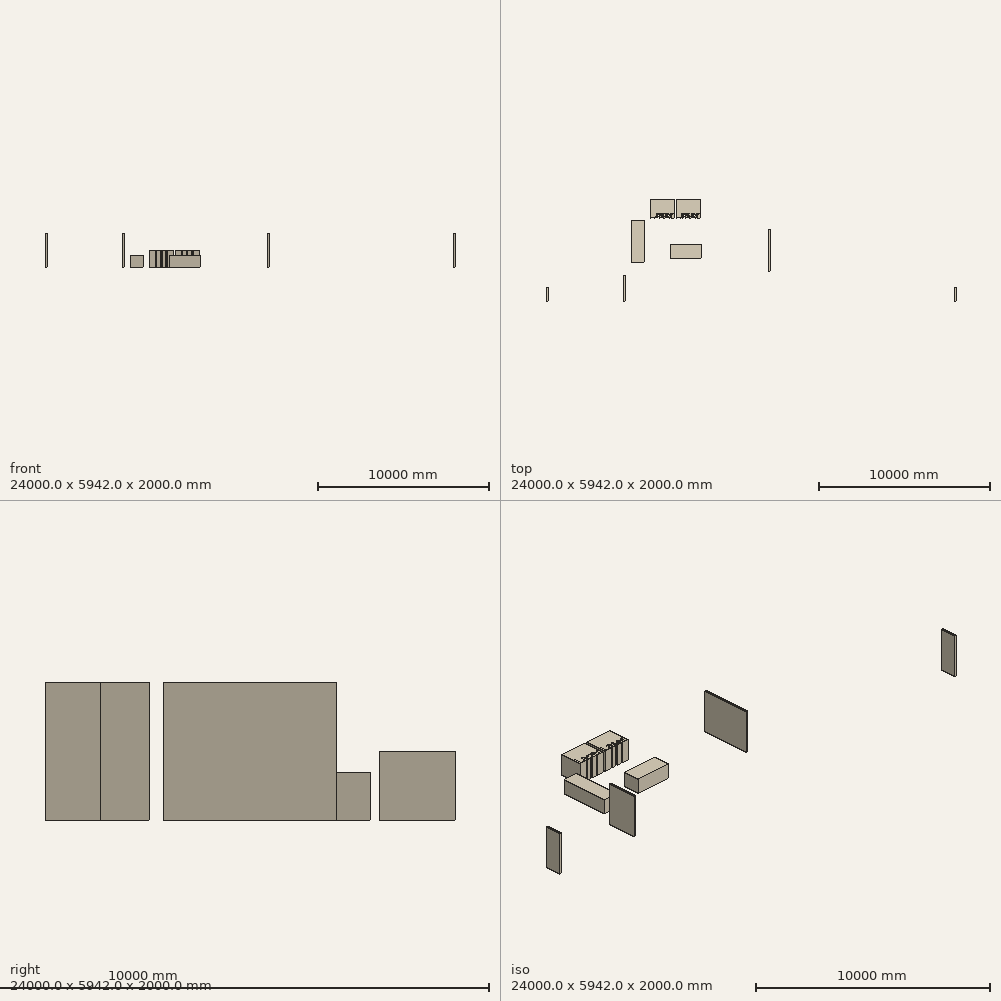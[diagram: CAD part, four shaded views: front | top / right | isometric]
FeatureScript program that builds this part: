
annotation { "Feature Type Name" : "Feature", "Feature Type Description" : "" }
export const myFeature = defineFeature(function(context is Context, id is Id, definition is map)
    precondition{}
    {
        {
            var Q0;
            Q0=qCreatedBy(makeId("Top.planeOp"),FACE);
            var sketch = newSketch(context, id + "F0", { "sketchPlane" : qUnion([Q0])});
            skLineSegment(sketch, "E0.bottom", {"start": v(-12000, 3350) * mm, "end": v(12000, 3350) * mm});
            skLineSegment(sketch, "E0.top", {"start": v(-12000, -3350) * mm, "end": v(12000, -3350) * mm});
            skLineSegment(sketch, "E0.left", {"start": v(-12000, 3350) * mm, "end": v(-12000, -3350) * mm});
            skLineSegment(sketch, "E0.right", {"start": v(12000, 3350) * mm, "end": v(12000, -3350) * mm});
            skPoint(sketch, "E0.middle", {"position": v(0, 0) * mm});
            skLineSegment(sketch, "E1.bottom", {"start": v(-11200, -3350) * mm, "end": v(-8700, -3350) * mm});
            skLineSegment(sketch, "E1.top", {"start": v(-11200, -3250) * mm, "end": v(-8700, -3250) * mm});
            skLineSegment(sketch, "E1.left", {"start": v(-11200, -3350) * mm, "end": v(-11200, -3250) * mm});
            skLineSegment(sketch, "E1.right", {"start": v(-8700, -3350) * mm, "end": v(-8700, -3250) * mm});
            skLineSegment(sketch, "E2.bottom", {"start": v(-12000, -2850) * mm, "end": v(-11900, -2850) * mm});
            skLineSegment(sketch, "E2.top", {"start": v(-12000, -2050) * mm, "end": v(-11900, -2050) * mm});
            skLineSegment(sketch, "E2.left", {"start": v(-12000, -2850) * mm, "end": v(-12000, -2050) * mm});
            skLineSegment(sketch, "E2.right", {"start": v(-11900, -2850) * mm, "end": v(-11900, -2050) * mm});
            skLineSegment(sketch, "E3.bottom", {"start": v(-11200, 3350) * mm, "end": v(-8700, 3350) * mm});
            skLineSegment(sketch, "E3.top", {"start": v(-11200, 3250) * mm, "end": v(-8700, 3250) * mm});
            skLineSegment(sketch, "E3.left", {"start": v(-11200, 3350) * mm, "end": v(-11200, 3250) * mm});
            skLineSegment(sketch, "E3.right", {"start": v(-8700, 3350) * mm, "end": v(-8700, 3250) * mm});
            skLineSegment(sketch, "E4.bottom", {"start": v(1200, -3350) * mm, "end": v(3700, -3350) * mm});
            skLineSegment(sketch, "E4.top", {"start": v(1200, -3250) * mm, "end": v(3700, -3250) * mm});
            skLineSegment(sketch, "E4.left", {"start": v(1200, -3350) * mm, "end": v(1200, -3250) * mm});
            skLineSegment(sketch, "E4.right", {"start": v(3700, -3350) * mm, "end": v(3700, -3250) * mm});
            skLineSegment(sketch, "E5.bottom", {"start": v(3900, -3350) * mm, "end": v(4700, -3350) * mm});
            skLineSegment(sketch, "E5.top", {"start": v(3900, -3250) * mm, "end": v(4700, -3250) * mm});
            skLineSegment(sketch, "E5.left", {"start": v(3900, -3350) * mm, "end": v(3900, -3250) * mm});
            skLineSegment(sketch, "E5.right", {"start": v(4700, -3350) * mm, "end": v(4700, -3250) * mm});
            skLineSegment(sketch, "E6.bottom", {"start": v(12000, -2050) * mm, "end": v(11900, -2050) * mm});
            skLineSegment(sketch, "E6.top", {"start": v(12000, -2850) * mm, "end": v(11900, -2850) * mm});
            skLineSegment(sketch, "E6.left", {"start": v(12000, -2050) * mm, "end": v(12000, -2850) * mm});
            skLineSegment(sketch, "E6.right", {"start": v(11900, -2050) * mm, "end": v(11900, -2850) * mm});
            skLineSegment(sketch, "E7", {"start": v(-7400, 3350) * mm, "end": v(-7400, -3350) * mm});
            skLineSegment(sketch, "E8", {"start": v(1000, 3350) * mm, "end": v(1000, -3350) * mm});
            skLineSegment(sketch, "E9.bottom", {"start": v(-3207.33, -2950.98) * mm, "end": v(-1707.33, -2950.98) * mm});
            skLineSegment(sketch, "E9.top", {"start": v(-3207.33, -1950.98) * mm, "end": v(-1707.33, -1950.98) * mm});
            skLineSegment(sketch, "E9.left", {"start": v(-3207.33, -2950.98) * mm, "end": v(-3207.33, -1950.98) * mm});
            skLineSegment(sketch, "E9.right", {"start": v(-1707.33, -2950.98) * mm, "end": v(-1707.33, -1950.98) * mm});
            skText(sketch, "E10", { "text": "Lathe", "fontName": "OpenSans-Regular.ttf"});
            skLineSegment(sketch, "E11.bottom", {"start": v(-5928.56, 3091.98) * mm, "end": v(-4528.56, 3091.98) * mm});
            skLineSegment(sketch, "E11.top", {"start": v(-5928.56, 1991.98) * mm, "end": v(-4528.56, 1991.98) * mm});
            skLineSegment(sketch, "E11.left", {"start": v(-5928.56, 3091.98) * mm, "end": v(-5928.56, 1991.98) * mm});
            skLineSegment(sketch, "E11.right", {"start": v(-4528.56, 3091.98) * mm, "end": v(-4528.56, 1991.98) * mm});
            skText(sketch, "E12", { "text": "Laser", "fontName": "OpenSans-Regular.ttf"});
            skLineSegment(sketch, "E13.bottom", {"start": v(-4412.76, 3091.98) * mm, "end": v(-3012.76, 3091.98) * mm});
            skLineSegment(sketch, "E13.top", {"start": v(-4412.76, 1991.98) * mm, "end": v(-3012.76, 1991.98) * mm});
            skLineSegment(sketch, "E13.left", {"start": v(-4412.76, 3091.98) * mm, "end": v(-4412.76, 1991.98) * mm});
            skLineSegment(sketch, "E13.right", {"start": v(-3012.76, 3091.98) * mm, "end": v(-3012.76, 1991.98) * mm});
            skText(sketch, "E14", { "text": "Laser", "fontName": "OpenSans-Regular.ttf"});
            skLineSegment(sketch, "E15.bottom", {"start": v(-1450.58, -1150.98) * mm, "end": v(549.42, -1150.98) * mm});
            skLineSegment(sketch, "E15.top", {"start": v(-1450.58, -2950.98) * mm, "end": v(549.42, -2950.98) * mm});
            skLineSegment(sketch, "E15.left", {"start": v(-1450.58, -1150.98) * mm, "end": v(-1450.58, -2950.98) * mm});
            skLineSegment(sketch, "E15.right", {"start": v(549.42, -1150.98) * mm, "end": v(549.42, -2950.98) * mm});
            skText(sketch, "E16", { "text": "Mill", "fontName": "OpenSans-Regular.ttf"});
            skLineSegment(sketch, "E17.bottom", {"start": v(-1450.58, -1150.98) * mm, "end": v(549.42, -1150.98) * mm, "construction": true});
            skLineSegment(sketch, "E17.top", {"start": v(-1450.58, 349.02) * mm, "end": v(549.42, 349.02) * mm, "construction": true});
            skLineSegment(sketch, "E17.left", {"start": v(-1450.58, -1150.98) * mm, "end": v(-1450.58, 349.02) * mm, "construction": true});
            skLineSegment(sketch, "E17.right", {"start": v(549.42, -1150.98) * mm, "end": v(549.42, 349.02) * mm, "construction": true});
            skLineSegment(sketch, "E18.bottom", {"start": v(-3207.33, -1950.98) * mm, "end": v(-1707.33, -1950.98) * mm, "construction": true});
            skLineSegment(sketch, "E18.top", {"start": v(-3207.33, -450.98) * mm, "end": v(-1707.33, -450.98) * mm, "construction": true});
            skLineSegment(sketch, "E18.left", {"start": v(-3207.33, -1950.98) * mm, "end": v(-3207.33, -450.98) * mm, "construction": true});
            skLineSegment(sketch, "E18.right", {"start": v(-1707.33, -1950.98) * mm, "end": v(-1707.33, -450.98) * mm, "construction": true});
            skLineSegment(sketch, "E19.bottom", {"start": v(-773.2, 3091.98) * mm, "end": v(726.8, 3091.98) * mm});
            skLineSegment(sketch, "E19.top", {"start": v(-773.2, 1591.98) * mm, "end": v(726.8, 1591.98) * mm});
            skLineSegment(sketch, "E19.left", {"start": v(-773.2, 3091.98) * mm, "end": v(-773.2, 1591.98) * mm});
            skLineSegment(sketch, "E19.right", {"start": v(726.8, 3091.98) * mm, "end": v(726.8, 1591.98) * mm});
            skLineSegment(sketch, "E20.bottom", {"start": v(-773.2, 1591.98) * mm, "end": v(726.8, 1591.98) * mm, "construction": true});
            skLineSegment(sketch, "E20.top", {"start": v(-773.2, 91.98) * mm, "end": v(726.8, 91.98) * mm, "construction": true});
            skLineSegment(sketch, "E20.left", {"start": v(-773.2, 1591.98) * mm, "end": v(-773.2, 91.98) * mm, "construction": true});
            skLineSegment(sketch, "E20.right", {"start": v(726.8, 1591.98) * mm, "end": v(726.8, 91.98) * mm, "construction": true});
            skText(sketch, "E21", { "text": "CNC", "fontName": "OpenSans-Regular.ttf"});
            skLineSegment(sketch, "E22.bottom", {"start": v(-6911.27, -2908.56) * mm, "end": v(-4472.87, -2908.56) * mm});
            skLineSegment(sketch, "E22.top", {"start": v(-6911.27, -2146.56) * mm, "end": v(-4472.87, -2146.56) * mm});
            skLineSegment(sketch, "E22.left", {"start": v(-6911.27, -2908.56) * mm, "end": v(-6911.27, -2146.56) * mm});
            skLineSegment(sketch, "E22.right", {"start": v(-4472.87, -2908.56) * mm, "end": v(-4472.87, -2146.56) * mm});
            skLineSegment(sketch, "E23.bottom", {"start": v(-7007.98, 1864.72) * mm, "end": v(-6245.98, 1864.72) * mm});
            skLineSegment(sketch, "E23.top", {"start": v(-7007.98, -573.68) * mm, "end": v(-6245.98, -573.68) * mm});
            skLineSegment(sketch, "E23.left", {"start": v(-7007.98, 1864.72) * mm, "end": v(-7007.98, -573.68) * mm});
            skLineSegment(sketch, "E23.right", {"start": v(-6245.98, 1864.72) * mm, "end": v(-6245.98, -573.68) * mm});
            skLineSegment(sketch, "E24.bottom", {"start": v(-2789.45, 3077.16) * mm, "end": v(-960.65, 3077.16) * mm});
            skLineSegment(sketch, "E24.top", {"start": v(-2789.45, 2315.16) * mm, "end": v(-960.65, 2315.16) * mm});
            skLineSegment(sketch, "E24.left", {"start": v(-2789.45, 3077.16) * mm, "end": v(-2789.45, 2315.16) * mm});
            skLineSegment(sketch, "E24.right", {"start": v(-960.65, 3077.16) * mm, "end": v(-960.65, 2315.16) * mm});
            skText(sketch, "E25", { "text": "Desk", "fontName": "OpenSans-Regular.ttf"});
            skText(sketch, "E26", { "text": "Chop", "fontName": "OpenSans-Regular.ttf"});
            skLineSegment(sketch, "E27.bottom", {"start": v(-4742.76, 474.12) * mm, "end": v(-2913.96, 474.12) * mm});
            skLineSegment(sketch, "E27.top", {"start": v(-4742.76, -338.68) * mm, "end": v(-2913.96, -338.68) * mm});
            skLineSegment(sketch, "E27.left", {"start": v(-4742.76, 474.12) * mm, "end": v(-4742.76, -338.68) * mm});
            skLineSegment(sketch, "E27.right", {"start": v(-2913.96, 474.12) * mm, "end": v(-2913.96, -338.68) * mm});
            skLineSegment(sketch, "E28.bottom", {"start": v(-7400, -1350) * mm, "end": v(-7500, -1350) * mm});
            skLineSegment(sketch, "E28.top", {"start": v(-7400, -2850) * mm, "end": v(-7500, -2850) * mm});
            skLineSegment(sketch, "E28.left", {"start": v(-7400, -1350) * mm, "end": v(-7400, -2850) * mm});
            skLineSegment(sketch, "E28.right", {"start": v(-7500, -1350) * mm, "end": v(-7500, -2850) * mm});
            skLineSegment(sketch, "E29.bottom", {"start": v(1000, 1365.62) * mm, "end": v(1100, 1365.62) * mm});
            skLineSegment(sketch, "E29.top", {"start": v(1000, -1134.38) * mm, "end": v(1100, -1134.38) * mm});
            skLineSegment(sketch, "E29.left", {"start": v(1000, 1365.62) * mm, "end": v(1000, -1134.38) * mm});
            skLineSegment(sketch, "E29.right", {"start": v(1100, 1365.62) * mm, "end": v(1100, -1134.38) * mm});
            skLineSegment(sketch, "E30.bottom", {"start": v(12000, -3350) * mm, "end": v(10500, -3350) * mm});
            skLineSegment(sketch, "E30.top", {"start": v(12000, -1850) * mm, "end": v(10500, -1850) * mm});
            skLineSegment(sketch, "E30.left", {"start": v(12000, -3350) * mm, "end": v(12000, -1850) * mm});
            skLineSegment(sketch, "E30.right", {"start": v(10500, -3350) * mm, "end": v(10500, -1850) * mm});
            skLineSegment(sketch, "E31.bottom", {"start": v(10500, -1850) * mm, "end": v(5500, -1850) * mm});
            skLineSegment(sketch, "E31.top", {"start": v(10500, -3350) * mm, "end": v(5500, -3350) * mm});
            skLineSegment(sketch, "E31.left", {"start": v(10500, -1850) * mm, "end": v(10500, -3350) * mm});
            skLineSegment(sketch, "E31.right", {"start": v(5500, -1850) * mm, "end": v(5500, -3350) * mm});
            skLineSegment(sketch, "E32", {"start": v(5800, -1850) * mm, "end": v(5800, -3350) * mm});
            skLineSegment(sketch, "E33.1.0.0", {"start": v(6100, -1850) * mm, "end": v(6100, -3350) * mm});
            skLineSegment(sketch, "E33.2.0.0", {"start": v(6400, -1850) * mm, "end": v(6400, -3350) * mm});
            skLineSegment(sketch, "E33.3.0.0", {"start": v(6700, -1850) * mm, "end": v(6700, -3350) * mm});
            skLineSegment(sketch, "E33.4.0.0", {"start": v(7000, -1850) * mm, "end": v(7000, -3350) * mm});
            skLineSegment(sketch, "E33.5.0.0", {"start": v(7300, -1850) * mm, "end": v(7300, -3350) * mm});
            skLineSegment(sketch, "E33.6.0.0", {"start": v(7600, -1850) * mm, "end": v(7600, -3350) * mm});
            skLineSegment(sketch, "E33.7.0.0", {"start": v(7900, -1850) * mm, "end": v(7900, -3350) * mm});
            skLineSegment(sketch, "E33.8.0.0", {"start": v(8200, -1850) * mm, "end": v(8200, -3350) * mm});
            skLineSegment(sketch, "E33.9.0.0", {"start": v(8500, -1850) * mm, "end": v(8500, -3350) * mm});
            skLineSegment(sketch, "E33.10.0.0", {"start": v(8800, -1850) * mm, "end": v(8800, -3350) * mm});
            skLineSegment(sketch, "E33.11.0.0", {"start": v(9100, -1850) * mm, "end": v(9100, -3350) * mm});
            skLineSegment(sketch, "E33.12.0.0", {"start": v(9400, -1850) * mm, "end": v(9400, -3350) * mm});
            skLineSegment(sketch, "E33.13.0.0", {"start": v(9700, -1850) * mm, "end": v(9700, -3350) * mm});
            skLineSegment(sketch, "E33.14.0.0", {"start": v(10000, -1850) * mm, "end": v(10000, -3350) * mm});
            skLineSegment(sketch, "E33.15.0.0", {"start": v(10300, -1850) * mm, "end": v(10300, -3350) * mm});
            skLineSegment(sketch, "E33.direction1", {"start": v(5800, -3350) * mm, "end": v(6100, -3350) * mm, "construction": true});
            skLineSegment(sketch, "E34.bottom", {"start": v(-8720.08, 3699.81) * mm, "end": v(-7720.08, 3699.81) * mm});
            skLineSegment(sketch, "E34.top", {"start": v(-8720.08, 2499.81) * mm, "end": v(-7720.08, 2499.81) * mm});
            skLineSegment(sketch, "E34.left", {"start": v(-8720.08, 3699.81) * mm, "end": v(-8720.08, 2499.81) * mm});
            skLineSegment(sketch, "E34.right", {"start": v(-7720.08, 3699.81) * mm, "end": v(-7720.08, 2499.81) * mm});
            skLineSegment(sketch, "E35.bottom", {"start": v(-8720.08, 2404.3) * mm, "end": v(-7720.08, 2404.3) * mm});
            skLineSegment(sketch, "E35.top", {"start": v(-8720.08, 1204.3) * mm, "end": v(-7720.08, 1204.3) * mm});
            skLineSegment(sketch, "E35.left", {"start": v(-8720.08, 2404.3) * mm, "end": v(-8720.08, 1204.3) * mm});
            skLineSegment(sketch, "E35.right", {"start": v(-7720.08, 2404.3) * mm, "end": v(-7720.08, 1204.3) * mm});
            skLineSegment(sketch, "E36.bottom", {"start": v(-8720.08, 1016.56) * mm, "end": v(-7720.08, 1016.56) * mm});
            skLineSegment(sketch, "E36.top", {"start": v(-8720.08, -307.1) * mm, "end": v(-7720.08, -307.1) * mm});
            skLineSegment(sketch, "E36.left", {"start": v(-8720.08, 1016.56) * mm, "end": v(-8720.08, -307.1) * mm});
            skLineSegment(sketch, "E36.right", {"start": v(-7720.08, 1016.56) * mm, "end": v(-7720.08, -307.1) * mm});
            skLineSegment(sketch, "E37.bottom", {"start": v(-6911.27, -2146.56) * mm, "end": v(-4472.87, -2146.56) * mm, "construction": true});
            skLineSegment(sketch, "E37.top", {"start": v(-6911.27, -646.56) * mm, "end": v(-4472.87, -646.56) * mm, "construction": true});
            skLineSegment(sketch, "E37.left", {"start": v(-6911.27, -2146.56) * mm, "end": v(-6911.27, -646.56) * mm, "construction": true});
            skLineSegment(sketch, "E37.right", {"start": v(-4472.87, -2146.56) * mm, "end": v(-4472.87, -646.56) * mm, "construction": true});
            skLineSegment(sketch, "E38.bottom", {"start": v(-5928.56, 1991.98) * mm, "end": v(-3012.76, 1991.98) * mm, "construction": true});
            skLineSegment(sketch, "E38.top", {"start": v(-5928.56, 491.98) * mm, "end": v(-3012.76, 491.98) * mm, "construction": true});
            skLineSegment(sketch, "E38.left", {"start": v(-5928.56, 1991.98) * mm, "end": v(-5928.56, 491.98) * mm, "construction": true});
            skLineSegment(sketch, "E38.right", {"start": v(-3012.76, 1991.98) * mm, "end": v(-3012.76, 491.98) * mm, "construction": true});
            skLineSegment(sketch, "E39.bottom", {"start": v(-6245.98, 1864.72) * mm, "end": v(-4745.98, 1864.72) * mm, "construction": true});
            skLineSegment(sketch, "E39.top", {"start": v(-6245.98, -573.68) * mm, "end": v(-4745.98, -573.68) * mm, "construction": true});
            skLineSegment(sketch, "E39.left", {"start": v(-6245.98, 1864.72) * mm, "end": v(-6245.98, -573.68) * mm, "construction": true});
            skLineSegment(sketch, "E39.right", {"start": v(-4745.98, 1864.72) * mm, "end": v(-4745.98, -573.68) * mm, "construction": true});
            const initialGuessF0  = {"E10": [-3.20733, -2.95098, 1, 0, 0.41293], "E12": [-5.92856, 1.99198, 1, 0, 0.39188], "E14": [-4.41276, 1.99198, 1, 0, 0.39188], "E16": [-1.45058, -2.95098, 1, 0, 0.87771], "E21": [-0.7732, 1.59198, 1, 0, 0.52663], "E25": [-2.78945, 2.31516, 1, 0, 0.4312], "E26": [-6.91127, -2.90856, 1, 0, 0.44352]};
            skSetInitialGuess(sketch, initialGuessF0);
            skSolve(sketch);
        }
        {
            var Q0;
            Q0=makeQuery(id+"F0.imprint","IMPRINT",FACE,{"disambiguationData":[TD([[makeQuery(id+"F0.imprint","IMPRINT",EDGE,{"derivedFrom":sQuery(id+"F0.wireOp",EDGE,"E3.bottom")}),-1.0]])]});
            var Q1;
            Q1=makeQuery(id+"F0.imprint","IMPRINT",FACE,{"disambiguationData":[TD([[makeQuery(id+"F0.imprint","IMPRINT",EDGE,{"derivedFrom":sQuery(id+"F0.wireOp",EDGE,"E2.bottom")}),1.0]])]});
            var Q2;
            Q2=makeQuery(id+"F0.imprint","IMPRINT",FACE,{"disambiguationData":[TD([[makeQuery(id+"F0.imprint","IMPRINT",EDGE,{"derivedFrom":sQuery(id+"F0.wireOp",EDGE,"E1.bottom")}),1.0]])]});
            var Q3;
            Q3=makeQuery(id+"F0.imprint","IMPRINT",FACE,{"disambiguationData":[TD([[makeQuery(id+"F0.imprint","IMPRINT",EDGE,{"derivedFrom":sQuery(id+"F0.wireOp",EDGE,"E5.bottom")}),1.0]])]});
            var Q4;
            Q4=makeQuery(id+"F0.imprint","IMPRINT",FACE,{"disambiguationData":[TD([[makeQuery(id+"F0.imprint","IMPRINT",EDGE,{"derivedFrom":sQuery(id+"F0.wireOp",EDGE,"E4.bottom")}),1.0]])]});
            var Q5;
            Q5=makeQuery(id+"F0.imprint","IMPRINT",FACE,{"disambiguationData":[TD([[makeQuery(id+"F0.imprint","IMPRINT",EDGE,{"derivedFrom":sQuery(id+"F0.wireOp",EDGE,"E6.bottom")}),1.0]])]});
            var Q6;
            Q6=makeQuery(id+"F0.imprint","IMPRINT",FACE,{"disambiguationData":[TD([[makeQuery(id+"F0.imprint","IMPRINT",EDGE,{"derivedFrom":sQuery(id+"F0.wireOp",EDGE,"E28.bottom")}),1.0]])]});
            var Q7;
            Q7=makeQuery(id+"F0.imprint","IMPRINT",FACE,{"disambiguationData":[TD([[makeQuery(id+"F0.imprint","IMPRINT",EDGE,{"derivedFrom":sQuery(id+"F0.wireOp",EDGE,"E29.bottom")}),-1.0]])]});
            extrude(context, id + "F1", {"entities" : qUnion([Q0, Q1, Q2, Q3, Q4, Q5, Q6, Q7]), "depth" : 2000 * mm, "offsetDistance" : 25 * mm});
        }
        {
            var Q0;
            Q0=sQuery(id+"F0.wireOp",EDGE,"E0.bottom");
            var Q1;
            Q1=sQuery(id+"F0.wireOp",EDGE,"E0.left");
            var Q2;
            Q2=sQuery(id+"F0.wireOp",EDGE,"E0.top");
            var Q3;
            Q3=sQuery(id+"F0.wireOp",EDGE,"E0.right");
            extrude(context, id + "F2", {"bodyType" : ToolBodyType.SURFACE, "surfaceEntities" : qUnion([Q0, Q1, Q2, Q3]), "depth" : 3000 * mm, "offsetDistance" : 25 * mm});
        }
        {
            var Q0;
            Q0=sQuery(id+"F0.wireOp",EDGE,"E7");
            var Q1;
            Q1=sQuery(id+"F0.wireOp",EDGE,"E8");
            extrude(context, id + "F3", {"bodyType" : ToolBodyType.SURFACE, "surfaceEntities" : qUnion([Q0, Q1]), "depth" : 3000 * mm, "offsetDistance" : 25 * mm});
        }
        {
            var Q0;
            Q0=makeQuery(id+"F0.imprint","IMPRINT",FACE,{"disambiguationData":[TD([[makeQuery(id+"F0.imprint","IMPRINT",EDGE,{"derivedFrom":sQuery(id+"F0.wireOp",EDGE,"E27.bottom")}),-1.0]])]});
            var Q1;
            Q1=makeQuery(id+"F0.imprint","IMPRINT",FACE,{"disambiguationData":[TD([[makeQuery(id+"F0.imprint","IMPRINT",EDGE,{"derivedFrom":sQuery(id+"F0.wireOp",EDGE,"E23.bottom")}),-1.0]])]});
            extrude(context, id + "F4", {"entities" : qUnion([Q0, Q1]), "depth" : 700 * mm, "offsetDistance" : 25 * mm});
        }
        {
            var Q0;
            Q0=makeQuery(id+"F0.imprint","IMPRINT",FACE,{"disambiguationData":[TD([[makeQuery(id+"F0.imprint","IMPRINT",EDGE,{"derivedFrom":sQuery(id+"F0.wireOp",EDGE,"E11.bottom")}),-1.0]])]});
            var Q1;
            Q1=makeQuery(id+"F0.imprint","IMPRINT",FACE,{"disambiguationData":[TD([[makeQuery(id+"F0.imprint","IMPRINT",EDGE,{"derivedFrom":sQuery(id+"F0.wireOp",EDGE,"E12.sketch_text.stroke-72")}),1.0]])]});
            var Q2;
            Q2=makeQuery(id+"F0.imprint","IMPRINT",FACE,{"disambiguationData":[TD([[makeQuery(id+"F0.imprint","IMPRINT",EDGE,{"derivedFrom":sQuery(id+"F0.wireOp",EDGE,"E12.sketch_text.stroke-25")}),1.0]])]});
            var Q3;
            {var subQ1=sQuery(id+"F0.wireOp",EDGE,"E12.sketch_text.stroke-6");Q3=makeQuery(id+"F0.imprint","IMPRINT",FACE,{"disambiguationData":[TD([[makeQuery(id+"F0.imprint","IMPRINT",EDGE,{"derivedFrom":subQ1}),1.0]])]});}
            var Q4;
            Q4=makeQuery(id+"F0.imprint","IMPRINT",FACE,{"disambiguationData":[TD([[makeQuery(id+"F0.imprint","IMPRINT",EDGE,{"derivedFrom":sQuery(id+"F0.wireOp",EDGE,"E13.bottom")}),-1.0]])]});
            var Q5;
            Q5=makeQuery(id+"F0.imprint","IMPRINT",FACE,{"disambiguationData":[TD([[makeQuery(id+"F0.imprint","IMPRINT",EDGE,{"derivedFrom":sQuery(id+"F0.wireOp",EDGE,"E14.sketch_text.stroke-25")}),1.0]])]});
            var Q6;
            {var subQ1=sQuery(id+"F0.wireOp",EDGE,"E14.sketch_text.stroke-6");Q6=makeQuery(id+"F0.imprint","IMPRINT",FACE,{"disambiguationData":[TD([[makeQuery(id+"F0.imprint","IMPRINT",EDGE,{"derivedFrom":subQ1}),1.0]])]});}
            var Q7;
            Q7=makeQuery(id+"F0.imprint","IMPRINT",FACE,{"disambiguationData":[TD([[makeQuery(id+"F0.imprint","IMPRINT",EDGE,{"derivedFrom":sQuery(id+"F0.wireOp",EDGE,"E14.sketch_text.stroke-72")}),1.0]])]});
            extrude(context, id + "F5", {"entities" : qUnion([Q0, Q1, Q2, Q3, Q4, Q5, Q6, Q7]), "depth" : 1000 * mm, "offsetDistance" : 25 * mm});
        }
    });
